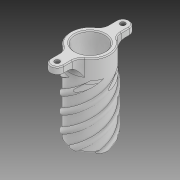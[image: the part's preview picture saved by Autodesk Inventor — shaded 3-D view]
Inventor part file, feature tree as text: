
AUTODESK INVENTOR PART (.ipt)
format: ipt  version: 2020 (Build 240168000, 168)  size: 737,280 bytes
history: native  units: mm
features: sketch x5, revolve x3, fillet x3, pattern_circular x2, other x1, helix x1, extrude x1, chamfer x1, projected_geometry x1
ambient origin geometry x8: Origin, YZ Plane, XZ Plane, XY Plane, X Axis, Y Axis, Z Axis, Center Point
bodies: Solid1 (feature_tree)
feature tree (18):
  revolve  "Revolution1"  [1 undecoded]
  revolve  "Revolution2"  [1 undecoded]
  pattern_circular  "Circular Pattern1"  [2 undecoded]
  sketch  "Sketch3"  dims[d4=90.0deg]
  other  "Work Axis1"
  helix  "Coil1"  [1 undecoded]
  pattern_circular  "Circular Pattern2"  Count=4 Angle=360.0deg
  revolve  "Revolution3"  [1 undecoded]
  fillet  "Fillet2"  Radius=1.5mm
  extrude  "Extrusion1"  Depth=3.0mm
  fillet  "Fillet3"  Radius=0.25mm
  fillet  "Fillet4"  Radius=50.0mm
  chamfer  "Chamfer1"  Distance=1.0mm
  sketch  "Sketch1"  dims[d0=25.0mm d1=4.2mm]
  sketch  "Sketch2"  dims[d2=4.525mm d3=1.475mm]
  projected_geometry  "Projected Loop1"
  sketch  "Sketch4"  dims[d5=0.25mm]
  sketch  "Sketch5"  dims[d6=2.0mm d7=1.3mm d8=90.0deg d9=40.0mm d10=360.0deg d13=6.0mm d14=1.5mm d15=0.75mm d16=0.25mm d17=25.0mm d18=10.0mm d19=7.5mm d20=0.0mm d21=90.0deg d22=90.0deg d23=0.0mm d24=0.0mm d25=50.0mm d26=360.0deg d28=1.0mm d29=1.745329mm d30=90.0deg d31=5.0mm d32=20.0mm d33=2.0mm d34=1.5mm d35=2.0mm d36=0.0mm d37=3.0mm d38=0.5mm d39=0.3mm d40=2.0mm d41=45.0deg]
note: 6 required parameter values undecoded (feature->parameter linkage not recoverable at this tier; creation-order binding heuristic only, values carry confidence <= 0.55)